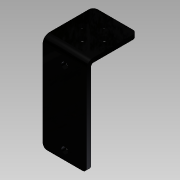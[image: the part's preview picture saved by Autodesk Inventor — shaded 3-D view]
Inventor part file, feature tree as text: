
AUTODESK INVENTOR PART (.ipt)
format: ipt  version: 2015 SP1 (Build 190203100, 203)  size: 143,872 bytes
history: native  units: mm
features: sketch x5, extrude x3, sweep x1, fillet x1, projected_geometry x1
ambient origin geometry x8: Origin, YZ Plane, XZ Plane, XY Plane, X Axis, Y Axis, Z Axis, Center Point
bodies: Solid1 (feature_tree)
feature tree (11):
  extrude  "Extrusion1"  Depth=20.0mm
  sweep  "Sweep1"
  extrude  "Extrusion2"  TaperAngle=0.0deg  [1 undecoded]
  fillet  "Fillet1"  Radius=20.0mm
  extrude  "Extrusion3"  Depth=3.0mm
  sketch  "Sketch1"  dims[d0=20.0mm d1=40.0mm]
  sketch  "Sketch2"  dims[d2=2.0mm d3=2.0mm d4=0.0mm]
  sketch  "Sketch3"  dims[d5=2.0mm d6=0.0mm d7=0.0mm d8=20.0mm]
  projected_geometry  "Projected Loop1"
  sketch  "Sketch4"  dims[d9=1.0mm d10=3.0mm]
  sketch  "Sketch5"  dims[d11=3.0mm d12=3.0mm d13=3.0mm d14=2.0mm d15=0.0mm d16=2.0mm d17=3.0mm d18=3.0mm d19=33.33mm d20=2.0mm d21=0.0mm]
note: 1 required parameter value undecoded (feature->parameter linkage not recoverable at this tier; creation-order binding heuristic only, values carry confidence <= 0.55)
